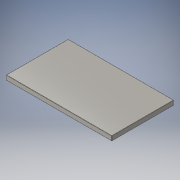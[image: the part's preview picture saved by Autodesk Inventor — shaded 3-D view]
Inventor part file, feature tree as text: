
AUTODESK INVENTOR PART (.ipt)
format: ipt  version: 2016 (Build 200138000, 138)  size: 130,560 bytes
history: native  units: mm
features: sheet_metal_op x4, sketch x2, other x2
ambient origin geometry x8: Origin, YZ Plane, XZ Plane, XY Plane, X Axis, Y Axis, Z Axis, Center Point
bodies: Solid1 (feature_tree)
feature tree (8):
  sheet_metal_op  "Face1"
  sheet_metal_op  "Flange1"
  sketch  "Sketch1"  dims[d0=1200.0mm]
  other  "Plate1"
  sketch  "Sketch2"  dims[d1=705.0mm d2=1.6mm d3=1.6mm d4=0.8mm d5=3.2mm d6=1.6mm d7=50.0mm d8=90.0deg d9=1.6mm d10=6.4mm d11=1.6mm d12=1.6mm]
  other  "Plate2"
  sheet_metal_op  "Bend1"
  sheet_metal_op  "Corner1"
